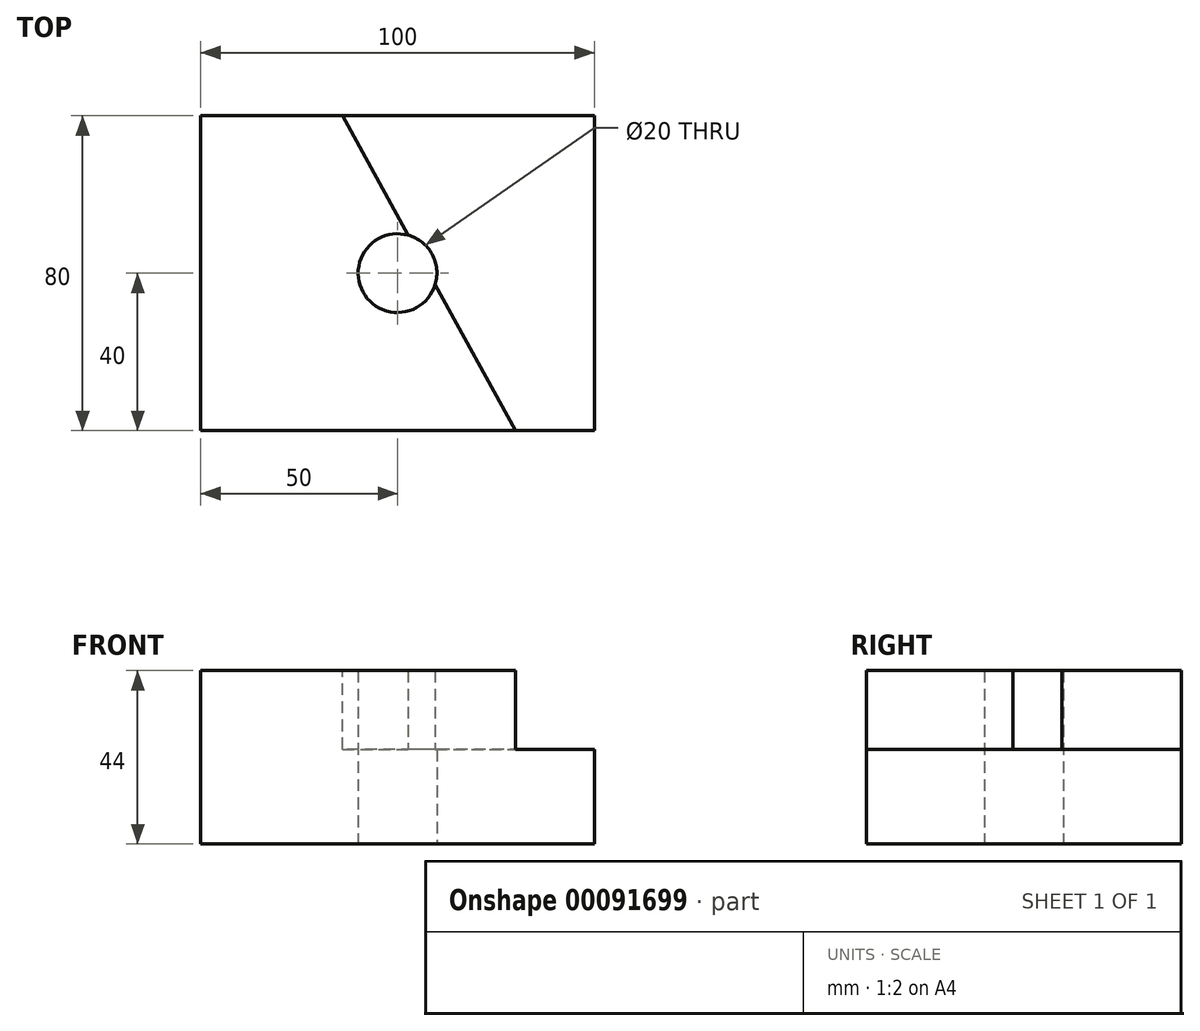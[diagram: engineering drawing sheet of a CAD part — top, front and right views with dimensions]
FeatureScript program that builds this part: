
annotation { "Feature Type Name" : "Feature", "Feature Type Description" : "" }
export const myFeature = defineFeature(function(context is Context, id is Id, definition is map)
    precondition{}
    {
        {
            var Q0;
            Q0=qCreatedBy(makeId("Top.planeOp"),FACE);
            var sketch = newSketch(context, id + "F0", { "sketchPlane" : qUnion([Q0])});
            skLineSegment(sketch, "E0.bottom", {"start": v(50, -40) * mm, "end": v(-50, -40) * mm});
            skLineSegment(sketch, "E0.top", {"start": v(50, 40) * mm, "end": v(-50, 40) * mm});
            skLineSegment(sketch, "E0.left", {"start": v(50, -40) * mm, "end": v(50, 40) * mm});
            skLineSegment(sketch, "E0.right", {"start": v(-50, -40) * mm, "end": v(-50, 40) * mm});
            skPoint(sketch, "E0.middle", {"position": v(0, 0) * mm});
            skCircle(sketch, "E1", {"center": v(0, 0) * mm, "radius": 10 * mm});
            skSolve(sketch);
        }
        {
            var Q0;
            Q0 = qSketchRegion(id + "F0", true);
            extrude(context, id + "F1", {"entities" : qUnion([Q0]), "depth" : 44 * mm});
        }
        {
            var Q0;
            Q0=makeQuery(id+"F1.opExtrude","CAP_FACE",FACE,{"disambiguationData":[OSD([sQuery(id+"F0.wireOp",EDGE,"E0.bottom"),sQuery(id+"F0.wireOp",EDGE,"E0.top"),sQuery(id+"F0.wireOp",EDGE,"E0.left"),sQuery(id+"F0.wireOp",EDGE,"E0.right"),sQuery(id+"F0.wireOp",EDGE,"E1")])],"isStart":false});
            var sketch = newSketch(context, id + "F2", { "sketchPlane" : qUnion([Q0])});
            skLineSegment(sketch, "E2.0", {"start": v(50, 40) * mm, "end": v(-14, 40) * mm});
            skLineSegment(sketch, "E3.0", {"start": v(50, -40) * mm, "end": v(50, 40) * mm});
            skLineSegment(sketch, "E4.0", {"start": v(50, -40) * mm, "end": v(30, -40) * mm});
            skLineSegment(sketch, "E5", {"start": v(-14, 40) * mm, "end": v(30, -40) * mm});
            skPoint(sketch, "E6.orphan", {"position": v(-50, -40) * mm});
            skPoint(sketch, "E7.orphan", {"position": v(-50, 40) * mm});
            skSolve(sketch);
        }
        {
            var Q0;
            Q0 = qSketchRegion(id + "F2", true);
            extrude(context, id + "F3", {"entities" : qUnion([Q0]), "operationType" : NewBodyOperationType.REMOVE, "oppositeDirection" : true, "depth" : 20 * mm});
        }
    });
